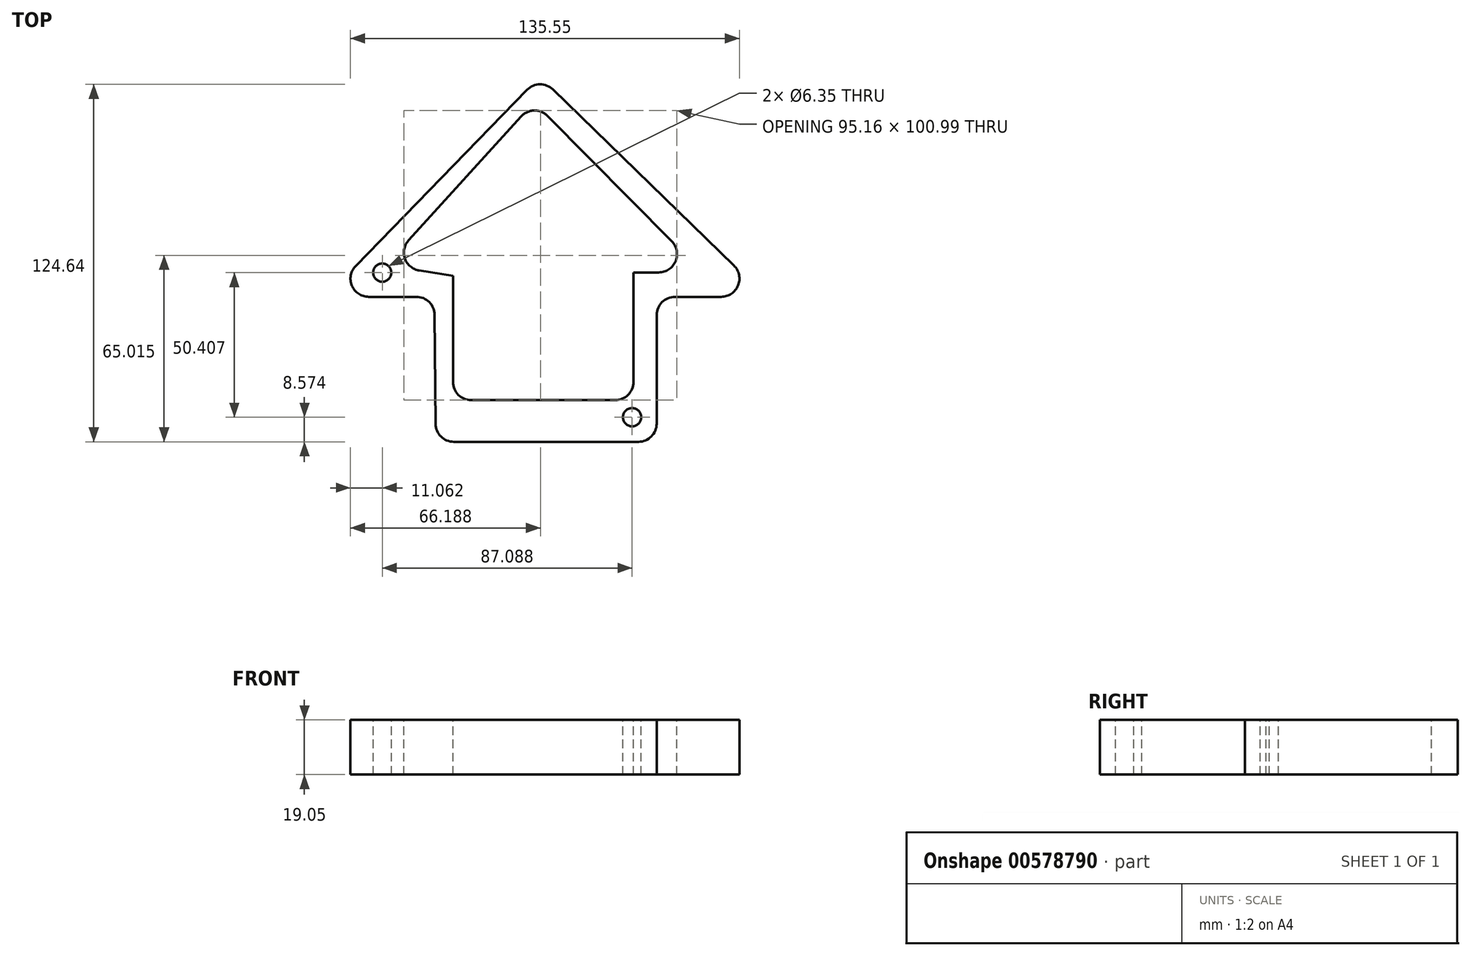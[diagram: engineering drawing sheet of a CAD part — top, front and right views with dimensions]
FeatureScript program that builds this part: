
annotation { "Feature Type Name" : "Feature", "Feature Type Description" : "" }
export const myFeature = defineFeature(function(context is Context, id is Id, definition is map)
    precondition{}
    {
        {
            var Q0;
            Q0=qCreatedBy(makeId("Top.planeOp"),FACE);
            var sketch = newSketch(context, id + "F0", { "sketchPlane" : qUnion([Q0])});
            skLineSegment(sketch, "E0", {"start": v(45.33, 2.9) * mm, "end": v(61.46, 2.9) * mm});
            skLineSegment(sketch, "E1", {"start": v(65.89, 13.8) * mm, "end": v(2.82, 75.2) * mm});
            skLineSegment(sketch, "E2", {"start": v(-6.16, 75.09) * mm, "end": v(-65.94, 13.69) * mm});
            skLineSegment(sketch, "E3", {"start": v(-61.39, 2.9) * mm, "end": v(-44.76, 2.9) * mm});
            skLineSegment(sketch, "E4", {"start": v(32.63, -47.63) * mm, "end": v(-31.74, -47.63) * mm});
            skLineSegment(sketch, "E5", {"start": v(-38.1, -41.34) * mm, "end": v(-38.4, -3.39) * mm});
            skLineSegment(sketch, "E6", {"start": v(38.98, -3.44) * mm, "end": v(38.98, -41.28) * mm});
            skPoint(sketch, "E7.visualSharp", {"position": v(77.08, 2.9) * mm});
            skArc(sketch, "E7.filletArc", {"start": v(61.46, 2.9) * mm, "mid": v(67.34, 6.87) * mm, "end": v(65.89, 13.8) * mm});
            skPoint(sketch, "E8.visualSharp", {"position": v(-76.43, 2.9) * mm});
            skArc(sketch, "E8.filletArc", {"start": v(-65.94, 13.69) * mm, "mid": v(-67.24, 6.8) * mm, "end": v(-61.39, 2.9) * mm});
            skPoint(sketch, "E9.visualSharp", {"position": v(-1.73, 79.64) * mm});
            skArc(sketch, "E9.filletArc", {"start": v(2.82, 75.2) * mm, "mid": v(-1.7, 77) * mm, "end": v(-6.16, 75.09) * mm});
            skPoint(sketch, "E10.visualSharp", {"position": v(-38.04, -47.63) * mm});
            skArc(sketch, "E10.filletArc", {"start": v(-38.1, -41.34) * mm, "mid": v(-36.21, -45.8) * mm, "end": v(-31.74, -47.63) * mm});
            skPoint(sketch, "E11.visualSharp", {"position": v(38.98, -47.63) * mm});
            skArc(sketch, "E11.filletArc", {"start": v(32.63, -47.63) * mm, "mid": v(37.12, -45.77) * mm, "end": v(38.98, -41.28) * mm});
            skPoint(sketch, "E12.visualSharp", {"position": v(-38.46, 2.9) * mm});
            skArc(sketch, "E12.filletArc", {"start": v(-38.4, -3.39) * mm, "mid": v(-40.29, 1.07) * mm, "end": v(-44.76, 2.9) * mm});
            skPoint(sketch, "E13.visualSharp", {"position": v(38.98, 2.9) * mm});
            skArc(sketch, "E13.filletArc", {"start": v(45.33, 2.9) * mm, "mid": v(40.84, 1.05) * mm, "end": v(38.98, -3.44) * mm});
            skSolve(sketch);
        }
        {
            var Q0;
            Q0=makeQuery(id+"F0.imprint","IMPRINT",FACE,{"disambiguationData":[TD([[makeQuery(id+"F0.imprint","IMPRINT",EDGE,{"derivedFrom":sQuery(id+"F0.wireOp",EDGE,"E0")}),1.0]])]});
            extrude(context, id + "F1", {"entities" : qUnion([Q0]), "depth" : 19.05 * mm, "offsetDistance" : 25.4 * mm});
        }
        {
            var Q0;
            Q0=makeQuery(id+"F1.opExtrude","CAP_FACE",FACE,{"disambiguationData":[OSD([sQuery(id+"F0.wireOp",EDGE,"E0"),sQuery(id+"F0.wireOp",EDGE,"E1"),sQuery(id+"F0.wireOp",EDGE,"E2"),sQuery(id+"F0.wireOp",EDGE,"E3"),sQuery(id+"F0.wireOp",EDGE,"E4"),sQuery(id+"F0.wireOp",EDGE,"E5"),sQuery(id+"F0.wireOp",EDGE,"E6"),sQuery(id+"F0.wireOp",EDGE,"E7.filletArc"),sQuery(id+"F0.wireOp",EDGE,"E8.filletArc"),sQuery(id+"F0.wireOp",EDGE,"E9.filletArc"),sQuery(id+"F0.wireOp",EDGE,"E10.filletArc"),sQuery(id+"F0.wireOp",EDGE,"E11.filletArc"),sQuery(id+"F0.wireOp",EDGE,"E12.filletArc"),sQuery(id+"F0.wireOp",EDGE,"E13.filletArc")])],"isStart":false});
            var sketch = newSketch(context, id + "F2", { "sketchPlane" : qUnion([Q0])});
            skSolve(sketch);
        }
        {
            var Q0;
            Q0=makeQuery(id+"F2.imprint","IMPRINT",FACE,{"disambiguationData":[TD([[makeQuery(id+"F2.imprint","IMPRINT",EDGE,{"derivedFrom":makeQuery(id+"F1.opExtrude","CAP_EDGE",EDGE,{"disambiguationData":[OSD([sQuery(id+"F0.wireOp",EDGE,"E0")])],"isStart":false})}),1.0]])]});
            var sketch = newSketch(context, id + "F3", { "sketchPlane" : qUnion([Q0])});
            skCircle(sketch, "E14", {"center": v(-56.68, 11.35) * mm, "radius": 3.18 * mm});
            skCircle(sketch, "E15", {"center": v(30.41, -39.06) * mm, "radius": 3.18 * mm});
            skSolve(sketch);
        }
        {
            var Q0;
            Q0 = qSketchRegion(id + "F3", true);
            extrude(context, id + "F4", {"entities" : qUnion([Q0]), "operationType" : NewBodyOperationType.REMOVE, "endBound" : BoundingType.THROUGH_ALL, "oppositeDirection" : true, "depth" : 25.4 * mm, "offsetDistance" : 25.4 * mm});
        }
        {
            var Q0;
            Q0=makeQuery(id+"F2.imprint","IMPRINT",FACE,{"disambiguationData":[TD([[makeQuery(id+"F2.imprint","IMPRINT",EDGE,{"derivedFrom":makeQuery(id+"F1.opExtrude","CAP_EDGE",EDGE,{"disambiguationData":[OSD([sQuery(id+"F0.wireOp",EDGE,"E0")])],"isStart":false})}),1.0]])]});
            var sketch = newSketch(context, id + "F5", { "sketchPlane" : qUnion([Q0])});
            skLineSegment(sketch, "E16", {"start": v(-47.5, 22.64) * mm, "end": v(-8.29, 65.8) * mm});
            skLineSegment(sketch, "E17", {"start": v(0.93, 66) * mm, "end": v(44.22, 22.25) * mm});
            skLineSegment(sketch, "E18", {"start": v(39.7, 11.44) * mm, "end": v(30.88, 11.44) * mm});
            skLineSegment(sketch, "E19", {"start": v(30.88, 11.44) * mm, "end": v(30.88, -26.76) * mm});
            skLineSegment(sketch, "E20", {"start": v(24.53, -33.1) * mm, "end": v(-25.65, -33.1) * mm});
            skLineSegment(sketch, "E21", {"start": v(-32, -26.76) * mm, "end": v(-32, 10.29) * mm});
            skLineSegment(sketch, "E22", {"start": v(-32, 10.29) * mm, "end": v(-43.76, 12.1) * mm});
            skPoint(sketch, "E23.visualSharp", {"position": v(-3.78, 70.76) * mm});
            skArc(sketch, "E23.filletArc", {"start": v(0.93, 66) * mm, "mid": v(-3.72, 67.88) * mm, "end": v(-8.29, 65.8) * mm});
            skPoint(sketch, "E24.visualSharp", {"position": v(-55.44, 13.9) * mm});
            skArc(sketch, "E24.filletArc", {"start": v(-47.5, 22.64) * mm, "mid": v(-48.78, 16.25) * mm, "end": v(-43.76, 12.1) * mm});
            skPoint(sketch, "E25.visualSharp", {"position": v(-32, -33.1) * mm});
            skArc(sketch, "E25.filletArc", {"start": v(-32, -26.76) * mm, "mid": v(-30.14, -31.25) * mm, "end": v(-25.65, -33.1) * mm});
            skPoint(sketch, "E26.visualSharp", {"position": v(30.88, -33.1) * mm});
            skArc(sketch, "E26.filletArc", {"start": v(24.53, -33.1) * mm, "mid": v(29.02, -31.25) * mm, "end": v(30.88, -26.76) * mm});
            skPoint(sketch, "E27.visualSharp", {"position": v(54.93, 11.44) * mm});
            skArc(sketch, "E27.filletArc", {"start": v(39.7, 11.44) * mm, "mid": v(45.57, 15.34) * mm, "end": v(44.22, 22.25) * mm});
            skSolve(sketch);
        }
        {
            var Q0;
            Q0 = qSketchRegion(id + "F5", true);
            extrude(context, id + "F6", {"entities" : qUnion([Q0]), "operationType" : NewBodyOperationType.REMOVE, "endBound" : BoundingType.THROUGH_ALL, "oppositeDirection" : true, "depth" : 25.4 * mm, "offsetDistance" : 25.4 * mm});
        }
    });
